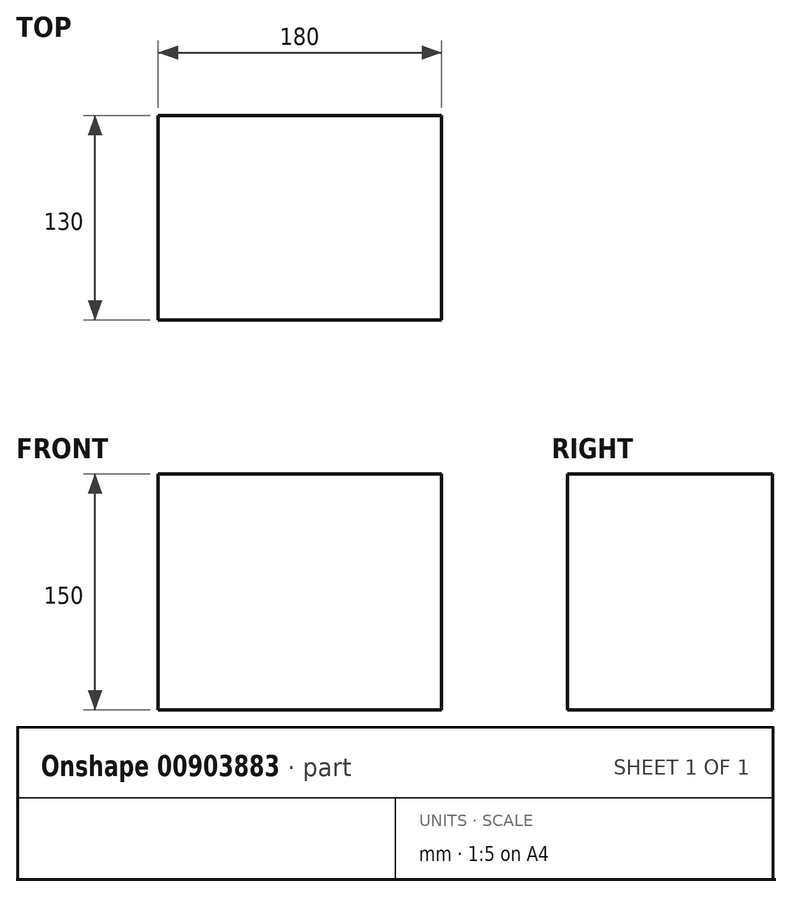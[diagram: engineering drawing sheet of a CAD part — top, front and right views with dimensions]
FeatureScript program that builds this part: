
annotation { "Feature Type Name" : "Feature", "Feature Type Description" : "" }
export const myFeature = defineFeature(function(context is Context, id is Id, definition is map)
    precondition{}
    {
        {
            var Q0;
            Q0=qCreatedBy(makeId("Top.planeOp"),FACE);
            var sketch = newSketch(context, id + "F0", { "sketchPlane" : qUnion([Q0])});
            skLineSegment(sketch, "E0.bottom", {"start": v(-90, 65) * mm, "end": v(90, 65) * mm});
            skLineSegment(sketch, "E0.top", {"start": v(-90, -65) * mm, "end": v(90, -65) * mm});
            skLineSegment(sketch, "E0.left", {"start": v(-90, 65) * mm, "end": v(-90, -65) * mm});
            skLineSegment(sketch, "E0.right", {"start": v(90, 65) * mm, "end": v(90, -65) * mm});
            skPoint(sketch, "E0.middle", {"position": v(0, 0) * mm});
            skSolve(sketch);
        }
        {
            var Q0;
            Q0 = qSketchRegion(id + "F0", true);
            extrude(context, id + "F1", {"entities" : qUnion([Q0]), "depth" : 150 * mm, "offsetDistance" : 25 * mm});
        }
    });
